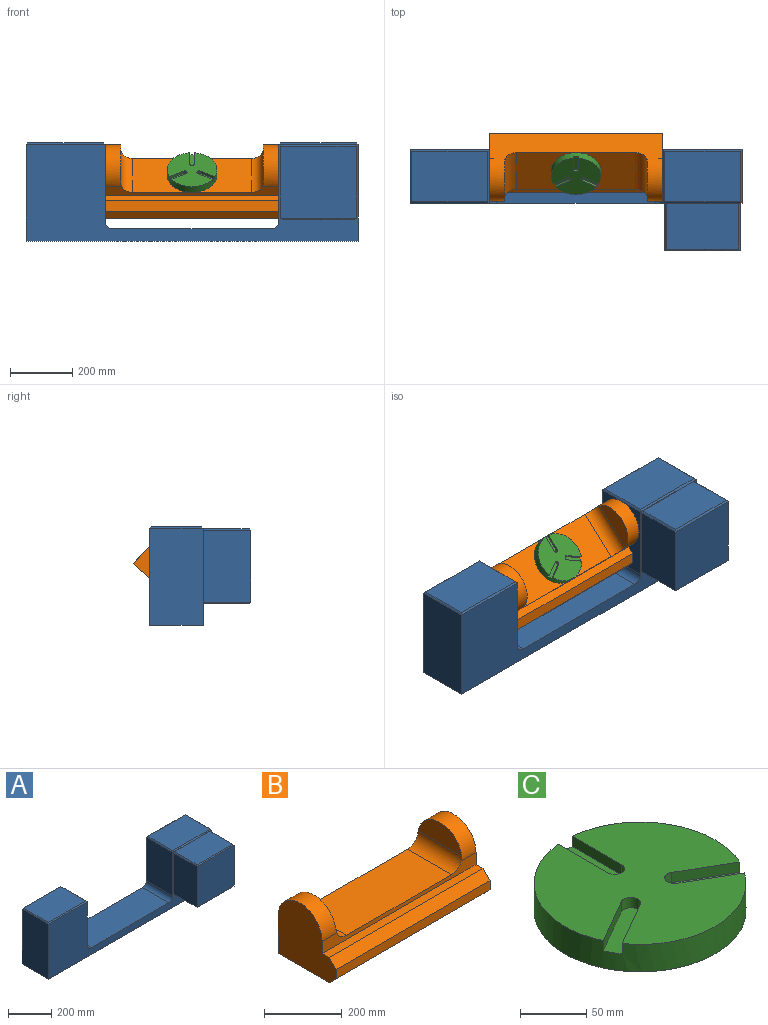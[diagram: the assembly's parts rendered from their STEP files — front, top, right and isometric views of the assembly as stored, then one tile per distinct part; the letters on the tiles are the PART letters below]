
ASSEMBLY  parts=3 mates=2
PART A: 31 faces, bbox 1066.8x325.1x316.2 mm
  f0: plane 243.84x162.56mm, normal (0,0,1), area 39638.6mm2, adj f23,f24,f25,f26
  f1: plane 1066.8x311.15mm, normal (0,-1,0), area 122166.2mm2, adj f3,f4,f6,f7,f8,f9,f10,f11
  f2: plane 1066.8x311.15mm, normal (0,1,0), area 180340.2mm2, adj f3,f4,f6,f7,f8,f9,f10,f11
  f3: plane 311.15x172.72mm, normal (1,0,0), area 53741.7mm2, adj f1,f2,f9,f26
  f4: plane 246.38x172.72mm, normal (-1,0,0), area 42554.8mm2, adj f1,f2,f10,f23
  f5: plane 243.84x162.56mm, normal (0,0,1), area 39638.6mm2, adj f27,f28,f29,f30
  f6: plane 311.15x172.72mm, normal (-1,0,0), area 53741.7mm2, adj f1,f2,f9,f28
  f7: plane 246.38x172.72mm, normal (1,0,0), area 42554.8mm2, adj f1,f2,f11,f29
  f8: plane 508x172.72mm, normal (0,0,1), area 87741.8mm2, adj f1,f2,f10,f11
  f9: plane 1066.8x172.72mm, normal (0,0,-1), area 184257.7mm2, adj f1,f2,f3,f6
  f10: cylinder r=25.4mm len=172.72mm, axis (0,1,0), area 6891.2mm2, adj f1,f2,f4,f8
  f11: cylinder r=25.4mm len=172.72mm, axis (0,1,0), area 6891.2mm2, adj f1,f2,f7,f8
  f12: plane 231.14x147.32mm, normal (0,0,1), area 34051.5mm2, adj f1,f20,f21,f22
  f13: plane 231.14x152.4mm, normal (-1,0,0), area 35225.7mm2, adj f1,f16,f17,f20
  f14: plane 231.14x147.32mm, normal (0,0,-1), area 34051.5mm2, adj f1,f17,f18,f19
  f15: plane 231.14x152.4mm, normal (1,0,0), area 35225.7mm2, adj f1,f16,f19,f22
  f16: plane 241.3x231.14mm, normal (0,-1,0), area 55774.1mm2, adj f13,f15,f18,f21
  f17: plane 152.4x5.08mm, normal (-0.71,0,-0.71), area 1076.6mm2, adj f1,f13,f14,f18
  f18: plane 241.3x5.08mm, normal (0,-0.71,-0.71), area 1697.1mm2, adj f14,f16,f17,f19
  f19: plane 152.4x5.08mm, normal (0.71,0,-0.71), area 1076.6mm2, adj f1,f14,f15,f18
  f20: plane 152.4x5.08mm, normal (-0.71,0,0.71), area 1076.6mm2, adj f1,f12,f13,f21
  f21: plane 241.3x5.08mm, normal (0,-0.71,0.71), area 1697.1mm2, adj f12,f16,f20,f22
  f22: plane 152.4x5.08mm, normal (0.71,0,0.71), area 1076.6mm2, adj f1,f12,f15,f21
  f23: plane 172.72x5.08mm, normal (-0.71,0,0.71), area 1204.4mm2, adj f0,f4,f24,f25
  f24: plane 254x5.08mm, normal (0,-0.71,0.71), area 1788.3mm2, adj f0,f1,f23,f26
  f25: plane 254x5.08mm, normal (0,0.71,0.71), area 1788.3mm2, adj f0,f2,f23,f26
  f26: plane 172.72x5.08mm, normal (0.71,0,0.71), area 1204.4mm2, adj f0,f3,f24,f25
  f27: plane 254x5.08mm, normal (0,-0.71,0.71), area 1788.3mm2, adj f1,f5,f28,f29
  f28: plane 172.72x5.08mm, normal (-0.71,0,0.71), area 1204.4mm2, adj f5,f6,f27,f30
  f29: plane 172.72x5.08mm, normal (0.71,0,0.71), area 1204.4mm2, adj f5,f7,f27,f30
  f30: plane 254x5.08mm, normal (0,0.71,0.71), area 1788.3mm2, adj f2,f5,f28,f29
PART B: 16 faces, bbox 558.8x210.8x197.6 mm
  f0: plane 558.8x38.1mm, normal (0,-1,0), area 10282.2mm2, adj f1,f5,f6,f8,f9,f10,f14,f15
  f1: plane 381x160.02mm, normal (0,0,1), area 60967.6mm2, adj f0,f2,f14,f15
  f2: plane 558.8x117.6mm, normal (0,1,0), area 54707.9mm2, adj f1,f3,f5,f6,f8,f9,f14,f15
  f3: plane 558.8x185.42mm, normal (0,0,-1), area 103612.7mm2, adj f2,f6,f9,f13
  f4: plane 157.99x67.31mm, normal (1,0,0), area 8031.9mm2, adj f5,f14
  f5: cylinder r=80.01mm len=160.02mm, axis (1,0,0), area 12787.3mm2, adj f0,f2,f4,f6,f14
  f6: plane 210.82x197.61mm, normal (-1,0,0), area 32267.8mm2, adj f0,f2,f3,f5,f10,f11,f12,f13
  f7: plane 157.99x67.31mm, normal (-1,0,0), area 8031.9mm2, adj f8,f15
  f8: cylinder r=80.01mm len=160.02mm, axis (-1,0,0), area 12787.3mm2, adj f0,f2,f7,f9,f15
  f9: plane 210.82x197.61mm, normal (1,0,0), area 32267.8mm2, adj f0,f2,f3,f8,f10,f11,f12,f13
  f10: plane 558.8x25.4mm, normal (0,0,1), area 14193.5mm2, adj f0,f6,f9,f11
  f11: plane 558.8x25.4mm, normal (0,-0.71,0.71), area 20072.7mm2, adj f6,f9,f10,f12
  f12: plane 558.8x28.7mm, normal (0,-1,0), area 16038.7mm2, adj f6,f9,f11,f13
  f13: plane 558.8x25.4mm, normal (0,-0.71,-0.71), area 20072.7mm2, adj f3,f6,f9,f12
  f14: cylinder r=38.1mm len=160.02mm, axis (0,1,0), area 9568.2mm2, adj f0,f1,f2,f4,f5
  f15: cylinder r=38.1mm len=160.02mm, axis (0,-1,0), area 9568.2mm2, adj f0,f1,f2,f7,f8
PART C: 15 faces, bbox 160x160x25.4 mm
  f0: cylinder r=80.01mm len=160.02mm, axis (0,0,1), area 12347.8mm2, adj f1,f2,f3,f5,f6,f7,f9,f10
  f1: plane 160.02x159.68mm, normal (0,0,1), area 17513.4mm2, adj f0,f3,f4,f5,f7,f8,f9,f11
  f2: plane 160.02x160.02mm, normal (0,0,-1), area 20111.2mm2, adj f0
  f3: plane 45.74x26.41mm, normal (-0.5,-0.87,0), area 503.1mm2, adj f0,f1,f4,f6
  f4: cylinder r=7.36mm len=13.73mm, axis (0,0,1), area 220.2mm2, adj f1,f3,f5,f6
  f5: plane 45.74x26.41mm, normal (0.5,0.87,0), area 503.1mm2, adj f0,f1,f4,f6
  f6: plane 56.78x40.14mm, normal (0,0,1), area 865.9mm2, adj f0,f3,f4,f5
  f7: plane 45.74x26.41mm, normal (-0.5,0.87,0), area 503.1mm2, adj f0,f1,f8,f10
  f8: cylinder r=7.36mm len=13.73mm, axis (0,0,1), area 220.2mm2, adj f1,f7,f9,f10
  f9: plane 45.74x26.41mm, normal (0.5,-0.87,0), area 503.1mm2, adj f0,f1,f8,f10
  f10: plane 56.78x40.14mm, normal (0,0,1), area 865.9mm2, adj f0,f7,f8,f9
  f11: plane 52.82x9.53mm, normal (1,0,0), area 503.1mm2, adj f0,f1,f12,f14
  f12: cylinder r=7.36mm len=14.72mm, axis (0,0,1), area 220.2mm2, adj f1,f11,f13,f14
  f13: plane 52.82x9.53mm, normal (-1,0,0), area 503.1mm2, adj f0,f1,f12,f14
  f14: plane 60.52x14.72mm, normal (0,0,1), area 865.9mm2, adj f0,f11,f12,f13
PLACE A t=(-11.05,-147.83,185.93)mm
PLACE B rot(axis=(1,0,0),42.9deg) t=(-11.05,-147.83,185.93)mm
PLACE C rot(axis=(1,0,0),42.9deg) t=(-11.05,-147.83,185.93)mm
MATE revolute A.f7 <-> B.f5  axis (1,0,0) through (-290.45,-147.83,185.93)mm
MATE revolute C.f0 <-> B.f1  axis (0,0.68,-0.73) through (-11.05,-130.54,167.33)mm
